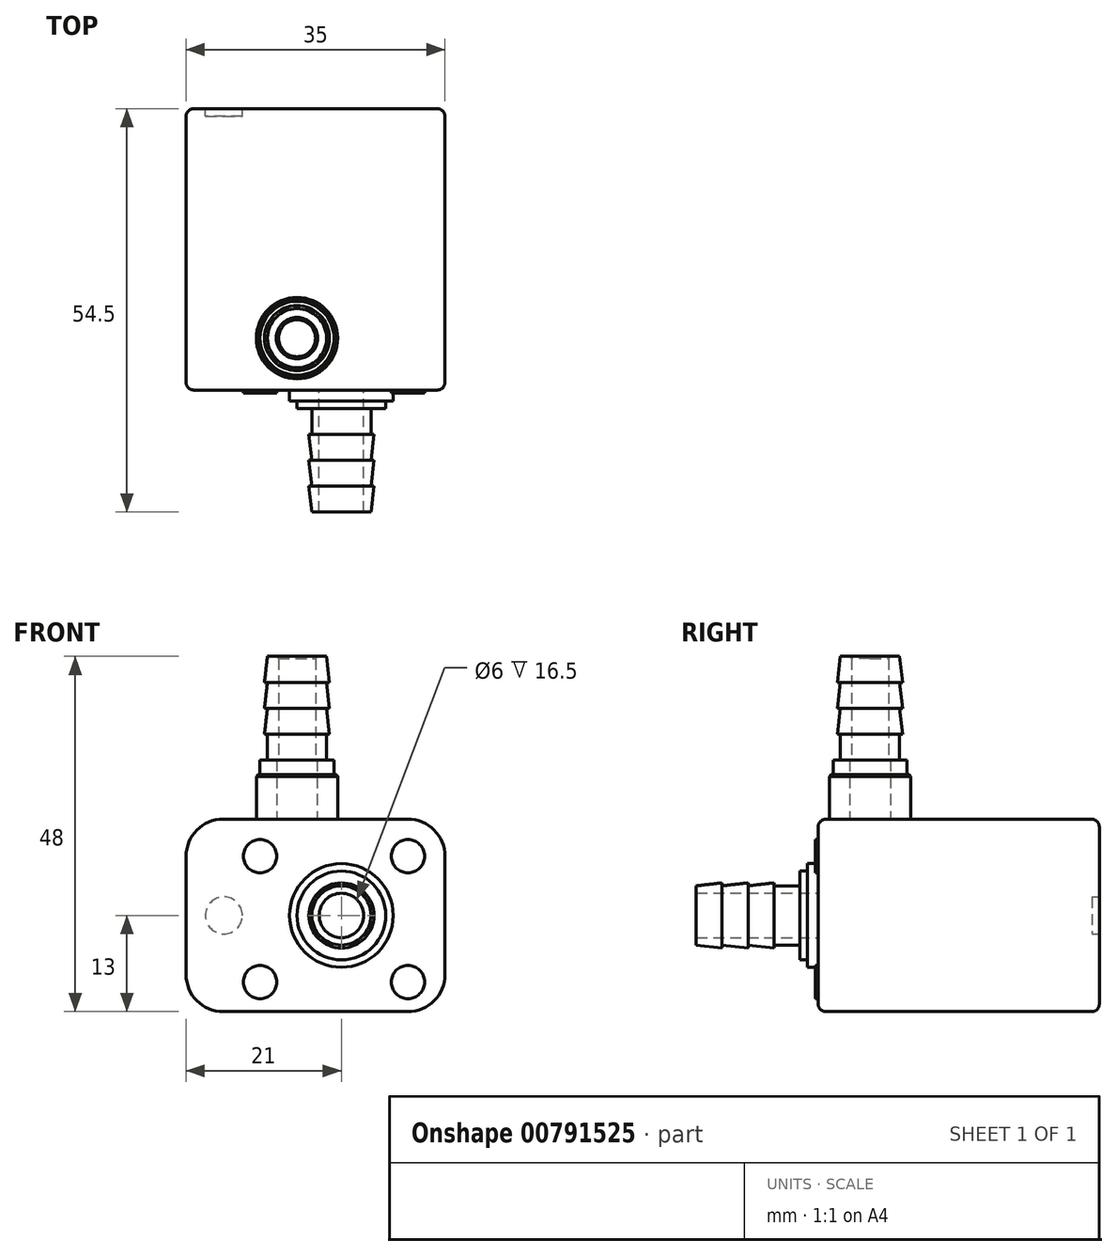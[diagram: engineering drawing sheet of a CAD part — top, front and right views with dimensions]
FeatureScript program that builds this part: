
annotation { "Feature Type Name" : "Feature", "Feature Type Description" : "" }
export const myFeature = defineFeature(function(context is Context, id is Id, definition is map)
    precondition{}
    {
        {
            var Q0;
            Q0=qCreatedBy(makeId("Top.planeOp"),FACE);
            var sketch = newSketch(context, id + "F0", { "sketchPlane" : qUnion([Q0])});
            skLineSegment(sketch, "E0.bottom", {"start": v(17.5, -19) * mm, "end": v(-17.5, -19) * mm});
            skLineSegment(sketch, "E0.top", {"start": v(17.5, 19) * mm, "end": v(-17.5, 19) * mm});
            skLineSegment(sketch, "E0.left", {"start": v(17.5, -19) * mm, "end": v(17.5, 19) * mm});
            skLineSegment(sketch, "E0.right", {"start": v(-17.5, -19) * mm, "end": v(-17.5, 19) * mm});
            skPoint(sketch, "E0.middle", {"position": v(0, 0) * mm});
            skSolve(sketch);
        }
        {
            var Q0;
            Q0=qSketchRegion(id+"F0",true);
            extrude(context, id + "F1", {"entities" : qUnion([Q0]), "depth" : 26 * mm});
        }
        {
            var Q0;
            Q0=makeQuery(id+"F1.opExtrude","CAP_FACE",FACE,{"disambiguationData":[OSD([sQuery(id+"F0.wireOp",EDGE,"E0.bottom"),sQuery(id+"F0.wireOp",EDGE,"E0.top"),sQuery(id+"F0.wireOp",EDGE,"E0.left"),sQuery(id+"F0.wireOp",EDGE,"E0.right")])],"isStart":false});
            var sketch = newSketch(context, id + "F2", { "sketchPlane" : qUnion([Q0])});
            skCircle(sketch, "E1", {"center": v(-2.5, -12) * mm, "radius": 5.5 * mm});
            skCircle(sketch, "E2", {"center": v(-2.5, -12) * mm, "radius": 2.75 * mm});
            skSolve(sketch);
        }
        {
            var Q0;
            Q0=qSketchRegion(id+"F2",true);
            extrude(context, id + "F3", {"entities" : qUnion([Q0]), "operationType" : NewBodyOperationType.ADD, "depth" : 6 * mm});
        }
        {
            var Q0;
            Q0=makeQuery(id+"F3.opExtrude","CAP_FACE",FACE,{"disambiguationData":[OSD([sQuery(id+"F2.wireOp",EDGE,"E1"),sQuery(id+"F2.wireOp",EDGE,"E2")])],"isStart":false});
            var sketch = newSketch(context, id + "F4", { "sketchPlane" : qUnion([Q0])});
            skCircle(sketch, "E3", {"center": v(-2.5, -12) * mm, "radius": 2.75 * mm});
            skCircle(sketch, "E4", {"center": v(-2.5, -12) * mm, "radius": 5 * mm});
            skSolve(sketch);
        }
        {
            var Q0;
            Q0=qSketchRegion(id+"F4",true);
            extrude(context, id + "F5", {"entities" : qUnion([Q0]), "operationType" : NewBodyOperationType.ADD, "depth" : 2 * mm});
        }
        {
            var Q0;
            Q0=qCreatedBy(makeId("Front.planeOp"),FACE);
            cPlane(context, id + "F6", {"entities" : qUnion([Q0]), "cplaneType" : CPlaneType.OFFSET, "offset" : 12 * mm, "width" : 150 * mm, "height" : 150 * mm});
        }
        {
            var Q0;
            Q0=qCreatedBy(id+"F6.planeOp",FACE);
            var sketch = newSketch(context, id + "F7", { "sketchPlane" : qUnion([Q0])});
            skLineSegment(sketch, "E5", {"start": v(-2.5, 34) * mm, "end": v(-2.5, 53.17) * mm, "construction": true});
            skLineSegment(sketch, "E6.0", {"start": v(-6.5, 34) * mm, "end": v(-6.5, 37.5) * mm});
            skLineSegment(sketch, "E7.0", {"start": v(-6.9, 34) * mm, "end": v(-6.9, 37.5) * mm, "construction": true});
            skLineSegment(sketch, "E8", {"start": v(-6.5, 37.5) * mm, "end": v(-6.9, 37.5) * mm});
            skLineSegment(sketch, "E9", {"start": v(-6.5, 41) * mm, "end": v(-6.9, 37.5) * mm});
            skLineSegment(sketch, "E10", {"start": v(-6.5, 41) * mm, "end": v(-6.9, 41) * mm});
            skLineSegment(sketch, "E11", {"start": v(-6.9, 41) * mm, "end": v(-6.5, 44.5) * mm});
            skLineSegment(sketch, "E12", {"start": v(-6.5, 44.5) * mm, "end": v(-6.9, 44.5) * mm});
            skLineSegment(sketch, "E13", {"start": v(-6.9, 44.5) * mm, "end": v(-6.5, 48) * mm});
            skLineSegment(sketch, "E14", {"start": v(-6.5, 48) * mm, "end": v(-5, 48) * mm});
            skLineSegment(sketch, "E15", {"start": v(-5, 48) * mm, "end": v(-5, 34) * mm});
            skLineSegment(sketch, "E16", {"start": v(-5, 34) * mm, "end": v(-6.5, 34) * mm});
            skSolve(sketch);
        }
        {
            var Q0;
            Q0=qSketchRegion(id+"F7",true);
            var Q1;
            Q1=sQuery(id+"F7.wireOp",EDGE,"E5");
            revolve(context, id + "F8", {"operationType" : NewBodyOperationType.ADD, "entities" : qUnion([Q0]), "axis" : qUnion([Q1]), "revolveType" : RevolveType.FULL});
        }
        {
            var Q0;
            Q0=makeQuery(id+"F8.opRevolve","SWEPT_EDGE",EDGE,{"disambiguationData":[OSD([sQuery(id+"F7.wireOp",EDGE,"E14"),sQuery(id+"F7.wireOp",EDGE,"E15")])]});
            chamfer(context, id + "F9", {"entities" : qUnion([Q0]), "width" : .3 * mm, "tangentPropagation" : true});
        }
        {
            var Q0;
            Q0=makeQuery(id+"F3.opExtrude","CAP_EDGE",EDGE,{"disambiguationData":[OSD([sQuery(id+"F2.wireOp",EDGE,"E1")])],"isStart":false});
            chamfer(context, id + "F10", {"entities" : qUnion([Q0]), "width" : .2 * mm, "tangentPropagation" : true});
        }
        {
            var Q0;
            Q0=makeQuery(id+"F1.opExtrude","CAP_EDGE",EDGE,{"disambiguationData":[OSD([sQuery(id+"F0.wireOp",EDGE,"E0.right")])],"isStart":false});
            var Q1;
            Q1=makeQuery(id+"F1.opExtrude","CAP_EDGE",EDGE,{"disambiguationData":[OSD([sQuery(id+"F0.wireOp",EDGE,"E0.right")])],"isStart":true});
            var Q2;
            Q2=makeQuery(id+"F1.opExtrude","CAP_EDGE",EDGE,{"disambiguationData":[OSD([sQuery(id+"F0.wireOp",EDGE,"E0.left")])],"isStart":false});
            var Q3;
            Q3=makeQuery(id+"F1.opExtrude","CAP_EDGE",EDGE,{"disambiguationData":[OSD([sQuery(id+"F0.wireOp",EDGE,"E0.left")])],"isStart":true});
            fillet(context, id + "F11", {"entities" : qUnion([Q0, Q1, Q2, Q3]), "radius" : 5 * mm, "tangentPropagation" : true, "allowEdgeOverflow" : false});
        }
        {
            var Q0;
            Q0=makeQuery(id+"F1.opExtrude","CAP_EDGE",EDGE,{"disambiguationData":[OSD([sQuery(id+"F0.wireOp",EDGE,"E0.top")])],"isStart":false});
            var Q1;
            Q1=makeQuery(id+"F1.opExtrude","CAP_EDGE",EDGE,{"disambiguationData":[OSD([sQuery(id+"F0.wireOp",EDGE,"E0.bottom")])],"isStart":false});
            fillet(context, id + "F12", {"entities" : qUnion([Q0, Q1]), "radius" : 1 * mm, "tangentPropagation" : true, "allowEdgeOverflow" : false});
        }
        {
            var Q0;
            Q0=makeQuery(id+"F1.opExtrude","SWEPT_FACE",FACE,{"disambiguationData":[OSD([sQuery(id+"F0.wireOp",EDGE,"E0.bottom")])]});
            var sketch = newSketch(context, id + "F13", { "sketchPlane" : qUnion([Q0])});
            skCircle(sketch, "E17", {"center": v(3.5, 13) * mm, "radius": 7 * mm});
            skCircle(sketch, "E18", {"center": v(3.5, 13) * mm, "radius": 3 * mm});
            skSolve(sketch);
        }
        {
            var Q0;
            Q0=qSketchRegion(id+"F13",true);
            extrude(context, id + "F14", {"entities" : qUnion([Q0]), "operationType" : NewBodyOperationType.ADD, "depth" : 1.5 * mm});
        }
        {
            var Q0;
            Q0=makeQuery(id+"F14.opExtrude","CAP_FACE",FACE,{"disambiguationData":[OSD([sQuery(id+"F13.wireOp",EDGE,"E17"),sQuery(id+"F13.wireOp",EDGE,"E18")])],"isStart":false});
            var sketch = newSketch(context, id + "F15", { "sketchPlane" : qUnion([Q0])});
            skCircle(sketch, "E19", {"center": v(3.5, 13) * mm, "radius": 3 * mm});
            skCircle(sketch, "E20", {"center": v(3.5, 13) * mm, "radius": 6 * mm});
            skSolve(sketch);
        }
        {
            var Q0;
            Q0=qSketchRegion(id+"F15",true);
            extrude(context, id + "F16", {"entities" : qUnion([Q0]), "operationType" : NewBodyOperationType.ADD, "depth" : 1 * mm});
        }
        {
            var Q0;
            Q0=qCreatedBy(makeId("Top.planeOp"),FACE);
            cPlane(context, id + "F17", {"entities" : qUnion([Q0]), "cplaneType" : CPlaneType.OFFSET, "offset" : 13 * mm, "width" : 150 * mm, "height" : 150 * mm});
        }
        {
            var Q0;
            Q0=qCreatedBy(id+"F17.planeOp",FACE);
            var sketch = newSketch(context, id + "F18", { "sketchPlane" : qUnion([Q0])});
            skLineSegment(sketch, "E21", {"start": v(3.5, -21.5) * mm, "end": v(3.5, -34.77) * mm, "construction": true});
            skLineSegment(sketch, "E22.0", {"start": v(0.5, -21.5) * mm, "end": v(0.5, -35.5) * mm});
            skLineSegment(sketch, "E23", {"start": v(0.5, -35.5) * mm, "end": v(-0.5, -35.5) * mm});
            skLineSegment(sketch, "E24", {"start": v(-0.5, -35.5) * mm, "end": v(-0.5, -26.45) * mm, "construction": true});
            skLineSegment(sketch, "E25.0", {"start": v(-0.9, -34.77) * mm, "end": v(-0.9, -22) * mm, "construction": true});
            skLineSegment(sketch, "E26.0", {"start": v(0.5, -32) * mm, "end": v(-0.5, -32) * mm, "construction": true});
            skLineSegment(sketch, "E27.0", {"start": v(0.5, -28.5) * mm, "end": v(-0.5, -28.5) * mm, "construction": true});
            skLineSegment(sketch, "E28.0", {"start": v(0.5, -25) * mm, "end": v(-0.5, -25) * mm, "construction": true});
            skLineSegment(sketch, "E29.0", {"start": v(0.5, -21.5) * mm, "end": v(-5.24, -21.5) * mm, "construction": true});
            skLineSegment(sketch, "E30", {"start": v(0.5, -21.5) * mm, "end": v(-5.24, -21.5) * mm});
            skLineSegment(sketch, "E31", {"start": v(-0.5, -25) * mm, "end": v(-0.9, -25) * mm});
            skLineSegment(sketch, "E32", {"start": v(-0.9, -25) * mm, "end": v(-0.5, -28.5) * mm});
            skLineSegment(sketch, "E33", {"start": v(-0.5, -28.5) * mm, "end": v(-0.9, -28.5) * mm});
            skLineSegment(sketch, "E34", {"start": v(-0.9, -28.5) * mm, "end": v(-0.5, -32) * mm});
            skLineSegment(sketch, "E35", {"start": v(-0.5, -32) * mm, "end": v(-0.9, -32) * mm});
            skLineSegment(sketch, "E36", {"start": v(-0.9, -32) * mm, "end": v(-0.5, -35.5) * mm});
            skLineSegment(sketch, "E37", {"start": v(-0.5, -25) * mm, "end": v(-0.5, -21.5) * mm});
            skLineSegment(sketch, "E38", {"start": v(-0.5, -21.5) * mm, "end": v(0.5, -21.5) * mm});
            skSolve(sketch);
        }
        {
            var Q0;
            Q0=qSketchRegion(id+"F18",true);
            var Q1;
            Q1=sQuery(id+"F18.wireOp",EDGE,"E21");
            revolve(context, id + "F19", {"operationType" : NewBodyOperationType.ADD, "entities" : qUnion([Q0]), "axis" : qUnion([Q1]), "revolveType" : RevolveType.FULL});
        }
        {
            var Q0;
            {var subQ0=sQuery(id+"F0.wireOp",EDGE,"E0.bottom");var subQ2=makeQuery(id+"F1.opExtrude","SWEPT_FACE",FACE,{"disambiguationData":[OSD([subQ0])]});Q0=makeQuery(id+"F14.boolean.opBoolean","SPLIT",FACE,{"disambiguationData":[TD([makeQuery(id+"F14.opExtrude","SWEPT_FACE",FACE,{"disambiguationData":[OSD([sQuery(id+"F13.wireOp",EDGE,"E17")])]})])],"derivedFrom":subQ2});}
            var sketch = newSketch(context, id + "F20", { "sketchPlane" : qUnion([Q0])});
            skCircle(sketch, "E39", {"center": v(-7.5, 21) * mm, "radius": 2.25 * mm});
            skCircle(sketch, "E40", {"center": v(12.5, 21) * mm, "radius": 2.25 * mm});
            skCircle(sketch, "E41", {"center": v(-7.5, 4) * mm, "radius": 2.25 * mm});
            skCircle(sketch, "E42", {"center": v(12.5, 4) * mm, "radius": 2.25 * mm});
            skSolve(sketch);
        }
        {
            var Q0;
            Q0=qSketchRegion(id+"F20",true);
            extrude(context, id + "F21", {"entities" : qUnion([Q0]), "operationType" : NewBodyOperationType.ADD, "depth" : .4 * mm});
        }
        {
            var Q0;
            Q0=makeQuery(id+"F1.opExtrude","SWEPT_FACE",FACE,{"disambiguationData":[OSD([sQuery(id+"F0.wireOp",EDGE,"E0.top")])]});
            var sketch = newSketch(context, id + "F22", { "sketchPlane" : qUnion([Q0])});
            skCircle(sketch, "E43", {"center": v(12.39, 13) * mm, "radius": 2.5 * mm});
            skPoint(sketch, "E43.centerSnap0", {"position": v(16.5, 13) * mm});
            skSolve(sketch);
        }
        {
            var Q0;
            Q0=qSketchRegion(id+"F22",true);
            extrude(context, id + "F23", {"entities" : qUnion([Q0]), "operationType" : NewBodyOperationType.REMOVE, "oppositeDirection" : true, "depth" : 1 * mm});
        }
    });
